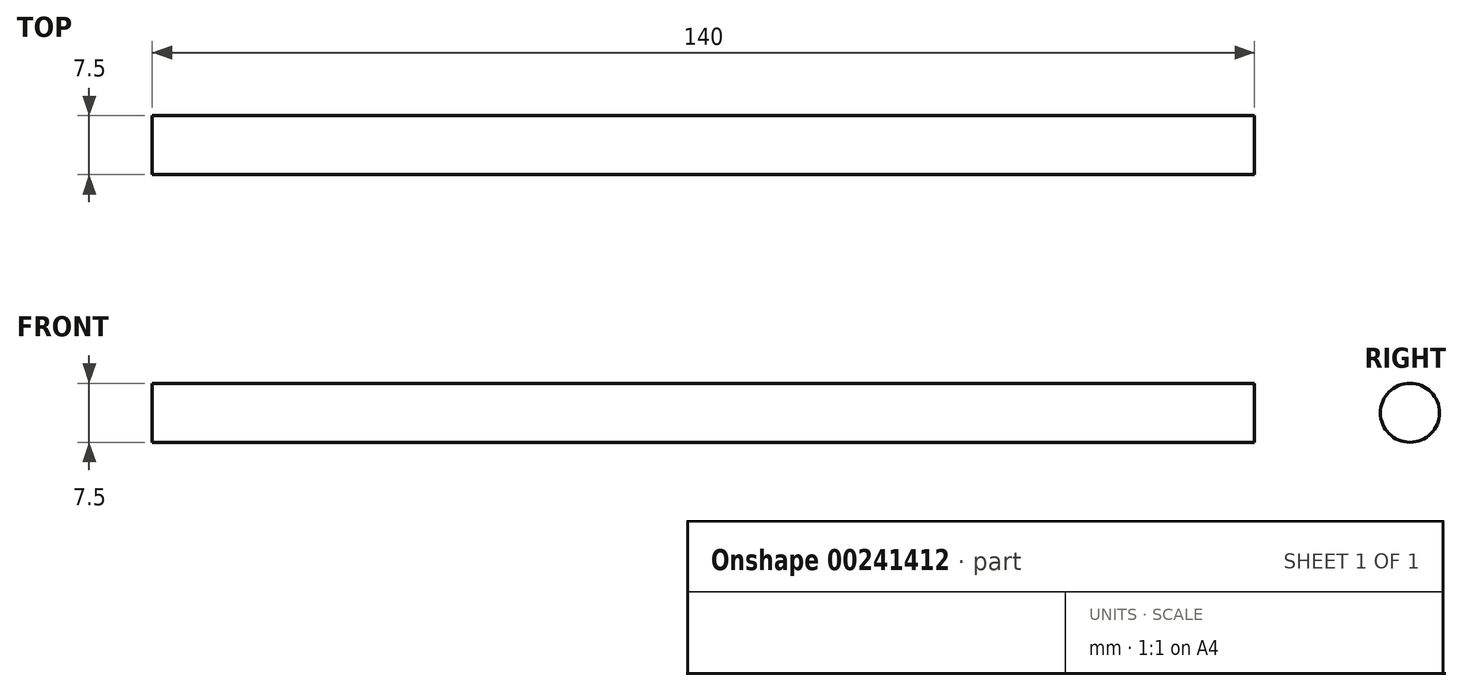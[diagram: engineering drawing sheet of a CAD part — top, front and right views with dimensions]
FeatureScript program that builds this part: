
annotation { "Feature Type Name" : "Feature", "Feature Type Description" : "" }
export const myFeature = defineFeature(function(context is Context, id is Id, definition is map)
    precondition{}
    {
        {
            var Q0;
            Q0=qCreatedBy(makeId("Right.planeOp"),FACE);
            var sketch = newSketch(context, id + "F0", { "sketchPlane" : qUnion([Q0])});
            skCircle(sketch, "E0", {"center": v(0, 0) * mm, "radius": 3.75 * mm});
            skSolve(sketch);
        }
        {
            var Q0;
            Q0 = qSketchRegion(id + "F0", true);
            extrude(context, id + "F1", {"entities" : qUnion([Q0]), "depth" : 140 * mm});
        }
    });
